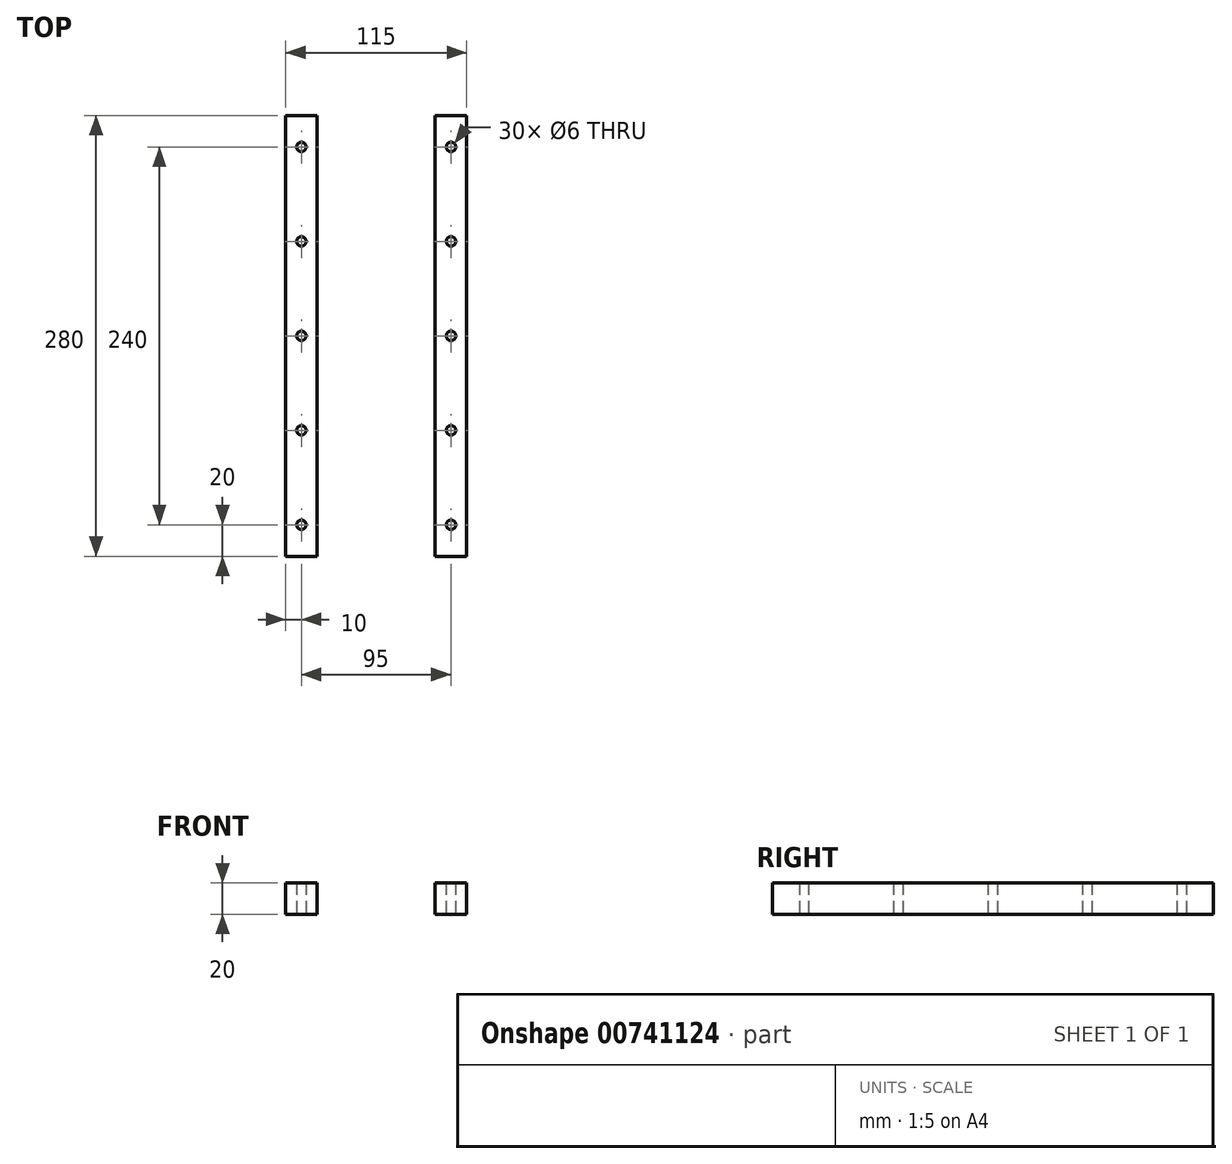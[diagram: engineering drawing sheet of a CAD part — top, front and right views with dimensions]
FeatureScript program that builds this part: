
annotation { "Feature Type Name" : "Feature", "Feature Type Description" : "" }
export const myFeature = defineFeature(function(context is Context, id is Id, definition is map)
    precondition{}
    {
        {
            var Q0;
            Q0=qCreatedBy(makeId("Top.planeOp"),FACE);
            var sketch = newSketch(context, id + "F0", { "sketchPlane" : qUnion([Q0])});
            skLineSegment(sketch, "E0.bottom", {"start": v(0, 0) * mm, "end": v(20, 0) * mm});
            skLineSegment(sketch, "E0.top", {"start": v(0, 280) * mm, "end": v(20, 280) * mm});
            skLineSegment(sketch, "E0.left", {"start": v(0, 0) * mm, "end": v(0, 280) * mm});
            skLineSegment(sketch, "E0.right", {"start": v(20, 0) * mm, "end": v(20, 280) * mm});
            skCircle(sketch, "E1", {"center": v(10, 20) * mm, "radius": 3 * mm});
            skLineSegment(sketch, "E2.direction1", {"start": v(10, 20) * mm, "end": v(35, 20) * mm, "construction": true});
            skCircle(sketch, "E3.0.1.0", {"center": v(10, 80) * mm, "radius": 3 * mm});
            skCircle(sketch, "E3.0.2.0", {"center": v(10, 140) * mm, "radius": 3 * mm});
            skCircle(sketch, "E3.0.3.0", {"center": v(10, 200) * mm, "radius": 3 * mm});
            skCircle(sketch, "E3.0.4.0", {"center": v(10, 260) * mm, "radius": 3 * mm});
            skLineSegment(sketch, "E3.direction2", {"start": v(10, 20) * mm, "end": v(10, 80) * mm, "construction": true});
            skLineSegment(sketch, "E4.1.0.0", {"start": v(105, 20) * mm, "end": v(105, 80) * mm, "construction": true});
            skLineSegment(sketch, "E4.1.0.1", {"start": v(115, 0) * mm, "end": v(115, 280) * mm});
            skLineSegment(sketch, "E4.1.0.2", {"start": v(95, 0) * mm, "end": v(95, 280) * mm});
            skLineSegment(sketch, "E4.1.0.3", {"start": v(95, 280) * mm, "end": v(115, 280) * mm});
            skLineSegment(sketch, "E4.1.0.4", {"start": v(95, 0) * mm, "end": v(115, 0) * mm});
            skCircle(sketch, "E4.1.0.5", {"center": v(105, 260) * mm, "radius": 3 * mm});
            skCircle(sketch, "E4.1.0.6", {"center": v(105, 200) * mm, "radius": 3 * mm});
            skCircle(sketch, "E4.1.0.7", {"center": v(105, 140) * mm, "radius": 3 * mm});
            skCircle(sketch, "E4.1.0.8", {"center": v(105, 80) * mm, "radius": 3 * mm});
            skCircle(sketch, "E4.1.0.9", {"center": v(105, 20) * mm, "radius": 3 * mm});
            skLineSegment(sketch, "E4.direction1", {"start": v(0, 0) * mm, "end": v(95, 0) * mm, "construction": true});
            skSolve(sketch);
        }
        {
            var Q0;
            Q0 = qSketchRegion(id + "F0", true);
            extrude(context, id + "F1", {"entities" : qUnion([Q0]), "depth" : 20 * mm, "offsetDistance" : 25 * mm});
        }
    });
